# Revit family: Electronics_Visual-TVs_ViewSonic_The-ViewSonicR-IFP8650-ViewBoard-Interac
name_source: partatom
category: Electrical Equipment
revit_build: Autodesk Revit 2015 (Build: 20140606_1530(x64)
units: mm (PartAtom-declared; Revit-internal decimal feet)

## types (1)
- IFP8650
    Assembly Code = D50
    BIMobject category = Visual - TVs
    BIMobject category code = electronics-visual-tvs
    BIMobject main category = Electronics
    BIMobject main category code = electronics
    BOSUseNativeGeometries = 1
    Brand url = https://www.viewsonic.com
    Color (front face) = Plastic - Viewsonic - Gray
    Covering Color = Plastic - Viewsonic - Black
    Description = Featuring 4K Ultra HD resolution and an immersive 20-point touch screen, the ViewSonic® ViewBoard® IFP8650 delivers incredible collaborative capabilities for 21st century boardrooms and classrooms. With astonishing 20-point simultaneous touch capabilities and pre-installed ViewSonic vBoard® annotation software, this 86” interactive flat panel lets multiple users write or draw on the screen with their fingers and styluses. With a built-in quad-core processor, as well as versatile connectivity options including multiple HDMI, VGA, RS232, RJ45, and USB ports, this display provides powerful computing for annotation and multimedia playback without the need for a PC. This display delivers optional slot-in PC capability, for more computing-intensive interactive applications. The IFP8650 features a VESA-compatible design and can be placed on a wall mount, or on an optional trolley cart for flexible installation in classrooms and corporate meeting rooms.
    Design country = Taiwan
    Edition number = 1
    Keynote = V90
    Manufacturer = ViewSonic
    Manufacturer country = Taiwan
    Manufacturer name = ViewSonic
    Model = viewsonic_ifp8650
    Product Guid = 34ec58bd-765e-4282-976b-00c96afcd0c0
    Product SKU = viewsonic_ifp8650
    Product data url = https://bimobject.com
    Product family = Electronics
    Product group = ViewBoard Interactive Flat Panel
    Product name = The ViewSonic® IFP8650 ViewBoard Interactive Flat Panel
    Product url = https://www.viewsonic.com
    QR code = http://bimobject.com
    URL = www.viewsonic.com

## geometry (parser evidence)
native form markers: Sweep x2
no freeform markers — native parametric forms only
